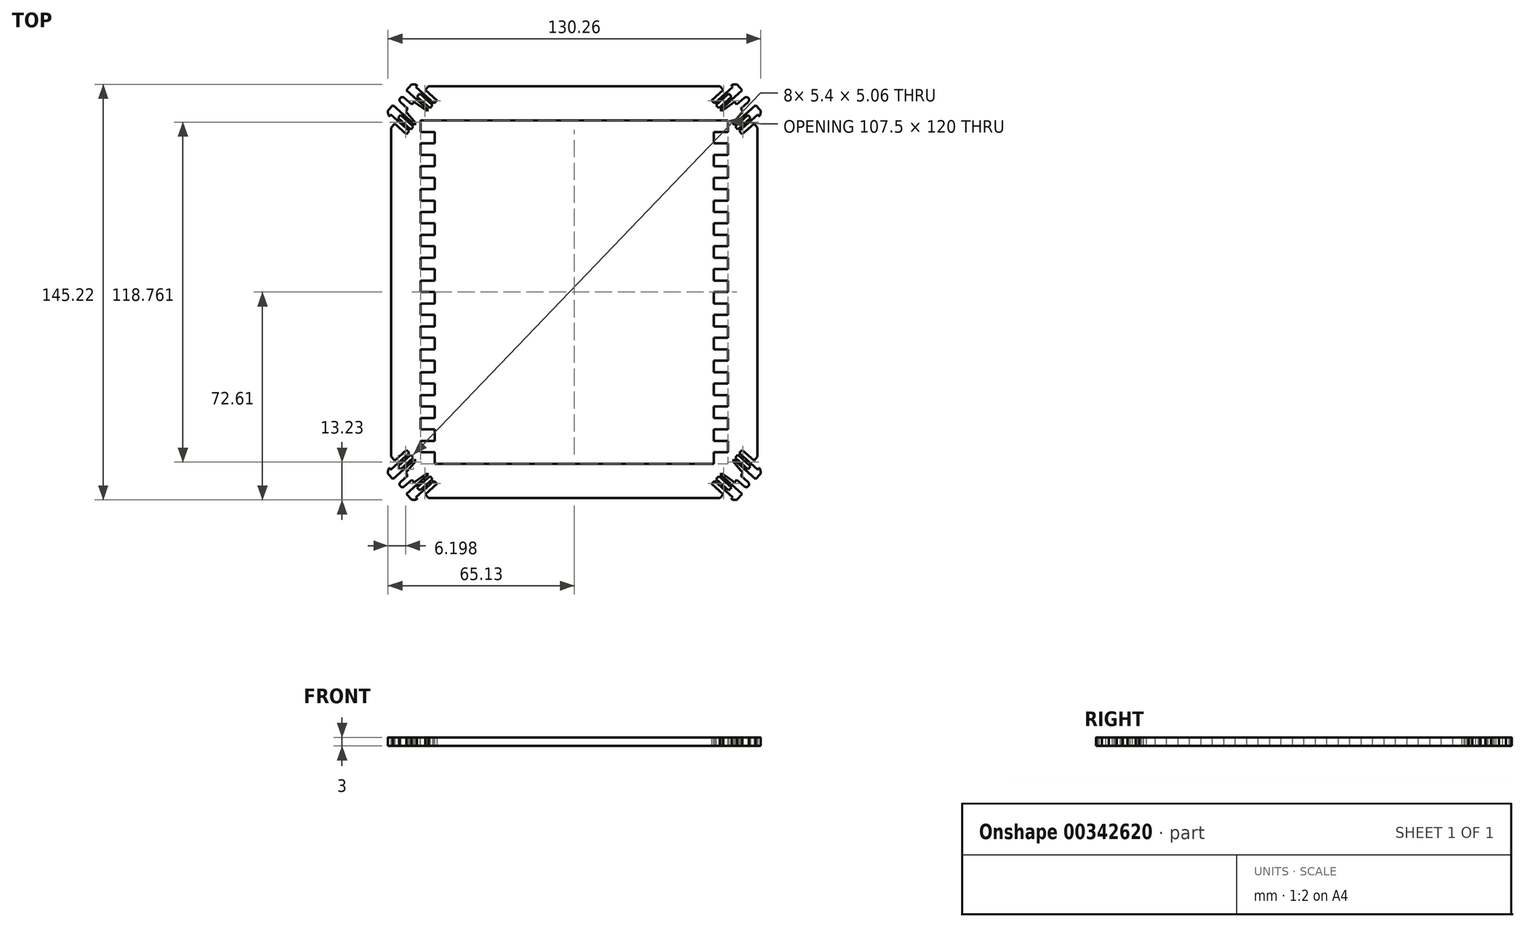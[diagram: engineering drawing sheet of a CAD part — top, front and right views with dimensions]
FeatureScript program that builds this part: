
annotation { "Feature Type Name" : "Feature", "Feature Type Description" : "" }
export const myFeature = defineFeature(function(context is Context, id is Id, definition is map)
    precondition{}
    {
        {
            var Q0;
            Q0=qCreatedBy(makeId("Top.planeOp"),FACE);
            var sketch = newSketch(context, id + "F0", { "sketchPlane" : qUnion([Q0])});
            skLineSegment(sketch, "E0", {"start": v(64, 57.49) * mm, "end": v(64, 0) * mm});
            skLineSegment(sketch, "E1", {"start": v(52.08, 70.72) * mm, "end": v(48, 67.04) * mm});
            skLineSegment(sketch, "E2", {"start": v(48, 67.04) * mm, "end": v(49, 65.92) * mm});
            skLineSegment(sketch, "E3", {"start": v(49, 65.92) * mm, "end": v(55.4, 71.67) * mm});
            skLineSegment(sketch, "E4", {"start": v(58.67, 70.58) * mm, "end": v(51.02, 63.69) * mm});
            skLineSegment(sketch, "E5", {"start": v(51.02, 63.69) * mm, "end": v(51.5, 63.29) * mm});
            skLineSegment(sketch, "E6", {"start": v(51.5, 63.29) * mm, "end": v(56, 66.46) * mm});
            skLineSegment(sketch, "E7", {"start": v(56, 66.46) * mm, "end": v(56.81, 65.55) * mm});
            skLineSegment(sketch, "E8", {"start": v(56.81, 65.55) * mm, "end": v(59.41, 67.89) * mm});
            skLineSegment(sketch, "E9", {"start": v(60.08, 67.15) * mm, "end": v(49.07, 57.23) * mm, "construction": true});
            skLineSegment(sketch, "E10.bottom", {"start": v(49.54, 65.32) * mm, "end": v(50.48, 64.28) * mm});
            skLineSegment(sketch, "E10.top", {"start": v(54, 69.34) * mm, "end": v(54.94, 68.3) * mm});
            skLineSegment(sketch, "E10.left", {"start": v(49.54, 65.32) * mm, "end": v(54, 69.34) * mm});
            skLineSegment(sketch, "E10.right", {"start": v(50.48, 64.28) * mm, "end": v(54.94, 68.3) * mm});
            skLineSegment(sketch, "E11", {"start": v(48, 67.04) * mm, "end": v(52.45, 62.1) * mm, "construction": true});
            skFitSpline(sketch, "E12", {"points": [v(55.4, 71.67) * mm, v(55, 72.26) * mm, v(56.93, 72.51) * mm], "startDerivative": vector(-1.28, 1.46) * mm, "endDerivative": vector(3.75, -1.07) * mm});
            skLineSegment(sketch, "E13", {"start": v(54.62, 75.08) * mm, "end": v(62.29, 66.57) * mm, "construction": true});
            skLineSegment(sketch, "E14", {"start": v(56.93, 72.51) * mm, "end": v(58.67, 70.58) * mm});
            skFitSpline(sketch, "E15.MirrorCS", {"points": [v(64.1, 62.01) * mm, v(64.64, 61.56) * mm, v(65.1, 63.45) * mm], "startDerivative": vector(1.32, -1.42) * mm, "endDerivative": vector(-0.67, 3.84) * mm});
            skLineSegment(sketch, "E16.MirrorCS", {"start": v(58.72, 55.14) * mm, "end": v(57.7, 56.26) * mm});
            skLineSegment(sketch, "E17.MirrorCS", {"start": v(57.17, 56.85) * mm, "end": v(56.23, 57.9) * mm});
            skLineSegment(sketch, "E18.MirrorCS", {"start": v(55.7, 58.49) * mm, "end": v(55.35, 59) * mm});
            skLineSegment(sketch, "E19.MirrorCS", {"start": v(58.72, 55.14) * mm, "end": v(54.27, 60.08) * mm, "construction": true});
            skLineSegment(sketch, "E20.MirrorCS", {"start": v(56.23, 57.9) * mm, "end": v(60.7, 61.9) * mm});
            skLineSegment(sketch, "E21.MirrorCS", {"start": v(62.8, 58.82) * mm, "end": v(58.72, 55.14) * mm});
            skLineSegment(sketch, "E22.MirrorCS", {"start": v(55.35, 59) * mm, "end": v(58.97, 63.15) * mm});
            skLineSegment(sketch, "E23.MirrorCS", {"start": v(63.35, 65.38) * mm, "end": v(55.7, 58.49) * mm});
            skLineSegment(sketch, "E24.MirrorCS", {"start": v(57.7, 56.26) * mm, "end": v(64.1, 62.01) * mm});
            skLineSegment(sketch, "E25.MirrorCS", {"start": v(65.1, 63.45) * mm, "end": v(63.35, 65.38) * mm});
            skLineSegment(sketch, "E26.MirrorCS", {"start": v(58.15, 64.06) * mm, "end": v(60.75, 66.4) * mm});
            skLineSegment(sketch, "E27.MirrorCS", {"start": v(61.63, 60.87) * mm, "end": v(60.7, 61.9) * mm});
            skLineSegment(sketch, "E28.MirrorCS", {"start": v(58.97, 63.15) * mm, "end": v(58.15, 64.06) * mm});
            skLineSegment(sketch, "E29.MirrorCS", {"start": v(57.17, 56.85) * mm, "end": v(61.63, 60.87) * mm});
            skArc(sketch, "E30", {"start": v(59.41, 67.89) * mm, "mid": v(60.83, 67.81) * mm, "end": v(60.75, 66.4) * mm});
            skLineSegment(sketch, "E31.0", {"start": v(54.62, 75.08) * mm, "end": v(56.93, 72.51) * mm, "construction": true});
            skLineSegment(sketch, "E32.0", {"start": v(51.5, 63.29) * mm, "end": v(52.45, 62.1) * mm, "construction": true});
            skLineSegment(sketch, "E33", {"start": v(50.93, 72) * mm, "end": v(0, 72) * mm});
            skLineSegment(sketch, "E34", {"start": v(0, 72) * mm, "end": v(0, 0) * mm});
            skLineSegment(sketch, "E35", {"start": v(0, 0) * mm, "end": v(64, 0) * mm});
            skLineSegment(sketch, "E36", {"start": v(52.08, 70.72) * mm, "end": v(50.93, 72) * mm});
            skLineSegment(sketch, "E37", {"start": v(62.8, 58.82) * mm, "end": v(64, 57.49) * mm});
            skSolve(sketch);
        }
        {
            var Q0;
            Q0 = qSketchRegion(id + "F0", true);
            extrude(context, id + "F1", {"entities" : qUnion([Q0]), "depth" : 3 * mm});
        }
        {
            var Q0;
            Q0=makeQuery(id+"F1.opExtrude","SWEPT_BODY",BODY,{"disambiguationData":[OSD([sQuery(id+"F0.wireOp",EDGE,"E0"),sQuery(id+"F0.wireOp",EDGE,"E1"),sQuery(id+"F0.wireOp",EDGE,"E2"),sQuery(id+"F0.wireOp",EDGE,"E3"),sQuery(id+"F0.wireOp",EDGE,"E4"),sQuery(id+"F0.wireOp",EDGE,"E5"),sQuery(id+"F0.wireOp",EDGE,"E6"),sQuery(id+"F0.wireOp",EDGE,"E7"),sQuery(id+"F0.wireOp",EDGE,"E8"),sQuery(id+"F0.wireOp",EDGE,"E10.bottom"),sQuery(id+"F0.wireOp",EDGE,"E10.top"),sQuery(id+"F0.wireOp",EDGE,"E10.left"),sQuery(id+"F0.wireOp",EDGE,"E10.right"),sQuery(id+"F0.wireOp",EDGE,"E12"),sQuery(id+"F0.wireOp",EDGE,"E14"),sQuery(id+"F0.wireOp",EDGE,"E15.MirrorCS"),sQuery(id+"F0.wireOp",EDGE,"E16.MirrorCS"),sQuery(id+"F0.wireOp",EDGE,"E17.MirrorCS"),sQuery(id+"F0.wireOp",EDGE,"E18.MirrorCS"),sQuery(id+"F0.wireOp",EDGE,"73c64eb1-9053-4ded-a230-a61976290448.MirrorCS"),sQuery(id+"F0.wireOp",EDGE,"E20.MirrorCS"),sQuery(id+"F0.wireOp",EDGE,"E21.MirrorCS"),sQuery(id+"F0.wireOp",EDGE,"E22.MirrorCS"),sQuery(id+"F0.wireOp",EDGE,"E23.MirrorCS"),sQuery(id+"F0.wireOp",EDGE,"E24.MirrorCS"),sQuery(id+"F0.wireOp",EDGE,"E25.MirrorCS"),sQuery(id+"F0.wireOp",EDGE,"E26.MirrorCS"),sQuery(id+"F0.wireOp",EDGE,"E27.MirrorCS"),sQuery(id+"F0.wireOp",EDGE,"E28.MirrorCS"),sQuery(id+"F0.wireOp",EDGE,"E29.MirrorCS"),sQuery(id+"F0.wireOp",EDGE,"E30"),sQuery(id+"F0.wireOp",EDGE,"238d3171-18cf-4664-875a-15b81accc3c9"),sQuery(id+"F0.wireOp",EDGE,"7124a334-57a5-4c12-b1ba-874bc8632110.MirrorC"),sQuery(id+"F0.wireOp",EDGE,"E33"),sQuery(id+"F0.wireOp",EDGE,"44bece61-ac72-4aae-9b04-1ec5777349d3"),sQuery(id+"F0.wireOp",EDGE,"E34"),sQuery(id+"F0.wireOp",EDGE,"E35")])]});
            var Q1;
            Q1=makeQuery(id+"F1.opExtrude","SWEPT_FACE",FACE,{"disambiguationData":[OSD([sQuery(id+"F0.wireOp",EDGE,"E34")])]});
            mirror(context, id + "F2", {"operationType" : NewBodyOperationType.ADD, "entities" : qUnion([Q0]), "mirrorPlane" : qUnion([Q1])});
        }
        {
            var Q0;
            Q0=makeQuery(id+"F1.opExtrude","SWEPT_BODY",BODY,{"disambiguationData":[OSD([sQuery(id+"F0.wireOp",EDGE,"E0"),sQuery(id+"F0.wireOp",EDGE,"E1"),sQuery(id+"F0.wireOp",EDGE,"E2"),sQuery(id+"F0.wireOp",EDGE,"E3"),sQuery(id+"F0.wireOp",EDGE,"E4"),sQuery(id+"F0.wireOp",EDGE,"E5"),sQuery(id+"F0.wireOp",EDGE,"E6"),sQuery(id+"F0.wireOp",EDGE,"E7"),sQuery(id+"F0.wireOp",EDGE,"E8"),sQuery(id+"F0.wireOp",EDGE,"E10.bottom"),sQuery(id+"F0.wireOp",EDGE,"E10.top"),sQuery(id+"F0.wireOp",EDGE,"E10.left"),sQuery(id+"F0.wireOp",EDGE,"E10.right"),sQuery(id+"F0.wireOp",EDGE,"E12"),sQuery(id+"F0.wireOp",EDGE,"E14"),sQuery(id+"F0.wireOp",EDGE,"E15.MirrorCS"),sQuery(id+"F0.wireOp",EDGE,"E16.MirrorCS"),sQuery(id+"F0.wireOp",EDGE,"E17.MirrorCS"),sQuery(id+"F0.wireOp",EDGE,"E18.MirrorCS"),sQuery(id+"F0.wireOp",EDGE,"73c64eb1-9053-4ded-a230-a61976290448.MirrorCS"),sQuery(id+"F0.wireOp",EDGE,"E20.MirrorCS"),sQuery(id+"F0.wireOp",EDGE,"E21.MirrorCS"),sQuery(id+"F0.wireOp",EDGE,"E22.MirrorCS"),sQuery(id+"F0.wireOp",EDGE,"E23.MirrorCS"),sQuery(id+"F0.wireOp",EDGE,"E24.MirrorCS"),sQuery(id+"F0.wireOp",EDGE,"E25.MirrorCS"),sQuery(id+"F0.wireOp",EDGE,"E26.MirrorCS"),sQuery(id+"F0.wireOp",EDGE,"E27.MirrorCS"),sQuery(id+"F0.wireOp",EDGE,"E28.MirrorCS"),sQuery(id+"F0.wireOp",EDGE,"E29.MirrorCS"),sQuery(id+"F0.wireOp",EDGE,"E30"),sQuery(id+"F0.wireOp",EDGE,"238d3171-18cf-4664-875a-15b81accc3c9"),sQuery(id+"F0.wireOp",EDGE,"7124a334-57a5-4c12-b1ba-874bc8632110.MirrorC"),sQuery(id+"F0.wireOp",EDGE,"E33"),sQuery(id+"F0.wireOp",EDGE,"44bece61-ac72-4aae-9b04-1ec5777349d3"),sQuery(id+"F0.wireOp",EDGE,"E34"),sQuery(id+"F0.wireOp",EDGE,"E35")])]});
            var Q1;
            {var subQ0=makeQuery(id+"F1.opExtrude","SWEPT_FACE",FACE,{"disambiguationData":[OSD([sQuery(id+"F0.wireOp",EDGE,"E35")])]});Q1=makeQuery(id+"F2.boolean.opBoolean","MERGE",FACE,{"derivedFrom":[subQ0,makeQuery(id+"F2.opPattern","COPY",FACE,{"derivedFrom":subQ0,"instanceName":"1"})]});}
            mirror(context, id + "F3", {"operationType" : NewBodyOperationType.ADD, "entities" : qUnion([Q0]), "mirrorPlane" : qUnion([Q1])});
        }
        {
            var Q0;
            {var subQ0=makeQuery(id+"F1.opExtrude","CAP_FACE",FACE,{"disambiguationData":[OSD([sQuery(id+"F0.wireOp",EDGE,"E0"),sQuery(id+"F0.wireOp",EDGE,"E1"),sQuery(id+"F0.wireOp",EDGE,"E2"),sQuery(id+"F0.wireOp",EDGE,"E3"),sQuery(id+"F0.wireOp",EDGE,"E4"),sQuery(id+"F0.wireOp",EDGE,"E5"),sQuery(id+"F0.wireOp",EDGE,"E6"),sQuery(id+"F0.wireOp",EDGE,"E7"),sQuery(id+"F0.wireOp",EDGE,"E8"),sQuery(id+"F0.wireOp",EDGE,"E10.bottom"),sQuery(id+"F0.wireOp",EDGE,"E10.top"),sQuery(id+"F0.wireOp",EDGE,"E10.left"),sQuery(id+"F0.wireOp",EDGE,"E10.right"),sQuery(id+"F0.wireOp",EDGE,"E12"),sQuery(id+"F0.wireOp",EDGE,"E14"),sQuery(id+"F0.wireOp",EDGE,"E15.MirrorCS"),sQuery(id+"F0.wireOp",EDGE,"E16.MirrorCS"),sQuery(id+"F0.wireOp",EDGE,"E17.MirrorCS"),sQuery(id+"F0.wireOp",EDGE,"E18.MirrorCS"),sQuery(id+"F0.wireOp",EDGE,"73c64eb1-9053-4ded-a230-a61976290448.MirrorCS"),sQuery(id+"F0.wireOp",EDGE,"E20.MirrorCS"),sQuery(id+"F0.wireOp",EDGE,"E21.MirrorCS"),sQuery(id+"F0.wireOp",EDGE,"E22.MirrorCS"),sQuery(id+"F0.wireOp",EDGE,"E23.MirrorCS"),sQuery(id+"F0.wireOp",EDGE,"E24.MirrorCS"),sQuery(id+"F0.wireOp",EDGE,"E25.MirrorCS"),sQuery(id+"F0.wireOp",EDGE,"E26.MirrorCS"),sQuery(id+"F0.wireOp",EDGE,"E27.MirrorCS"),sQuery(id+"F0.wireOp",EDGE,"E28.MirrorCS"),sQuery(id+"F0.wireOp",EDGE,"E29.MirrorCS"),sQuery(id+"F0.wireOp",EDGE,"E30"),sQuery(id+"F0.wireOp",EDGE,"238d3171-18cf-4664-875a-15b81accc3c9"),sQuery(id+"F0.wireOp",EDGE,"7124a334-57a5-4c12-b1ba-874bc8632110.MirrorC"),sQuery(id+"F0.wireOp",EDGE,"E33"),sQuery(id+"F0.wireOp",EDGE,"44bece61-ac72-4aae-9b04-1ec5777349d3"),sQuery(id+"F0.wireOp",EDGE,"E34"),sQuery(id+"F0.wireOp",EDGE,"E35")])],"isStart":false});var subQ1=makeQuery(id+"F2.boolean.opBoolean","MERGE",FACE,{"derivedFrom":[subQ0,makeQuery(id+"F2.opPattern","COPY",FACE,{"derivedFrom":subQ0,"instanceName":"1"})]});Q0=makeQuery(id+"F3.boolean.opBoolean","MERGE",FACE,{"derivedFrom":[subQ1,makeQuery(id+"F3.opPattern","COPY",FACE,{"derivedFrom":subQ1,"instanceName":"1"})]});}
            var sketch = newSketch(context, id + "F4", { "sketchPlane" : qUnion([Q0])});
            skLineSegment(sketch, "E38.bottom", {"start": v(53.75, 60) * mm, "end": v(-53.75, 60) * mm});
            skLineSegment(sketch, "E38.top", {"start": v(53.75, -60) * mm, "end": v(-53.75, -60) * mm});
            skLineSegment(sketch, "E38.left", {"start": v(53.75, 60) * mm, "end": v(53.75, -60) * mm});
            skLineSegment(sketch, "E38.right", {"start": v(-53.75, 60) * mm, "end": v(-53.75, -60) * mm});
            skPoint(sketch, "E38.middle", {"position": v(0, 0) * mm});
            skSolve(sketch);
        }
        {
            var Q0;
            Q0 = qSketchRegion(id + "F4", true);
            extrude(context, id + "F5", {"entities" : qUnion([Q0]), "operationType" : NewBodyOperationType.REMOVE, "oppositeDirection" : true, "depth" : 3 * mm});
        }
        {
            var Q0;
            {var subQ0=makeQuery(id+"F1.opExtrude","CAP_FACE",FACE,{"disambiguationData":[OSD([sQuery(id+"F0.wireOp",EDGE,"E0"),sQuery(id+"F0.wireOp",EDGE,"E1"),sQuery(id+"F0.wireOp",EDGE,"E2"),sQuery(id+"F0.wireOp",EDGE,"E3"),sQuery(id+"F0.wireOp",EDGE,"E4"),sQuery(id+"F0.wireOp",EDGE,"E5"),sQuery(id+"F0.wireOp",EDGE,"E6"),sQuery(id+"F0.wireOp",EDGE,"E7"),sQuery(id+"F0.wireOp",EDGE,"E8"),sQuery(id+"F0.wireOp",EDGE,"E10.bottom"),sQuery(id+"F0.wireOp",EDGE,"E10.top"),sQuery(id+"F0.wireOp",EDGE,"E10.left"),sQuery(id+"F0.wireOp",EDGE,"E10.right"),sQuery(id+"F0.wireOp",EDGE,"E12"),sQuery(id+"F0.wireOp",EDGE,"E14"),sQuery(id+"F0.wireOp",EDGE,"E15.MirrorCS"),sQuery(id+"F0.wireOp",EDGE,"E16.MirrorCS"),sQuery(id+"F0.wireOp",EDGE,"E17.MirrorCS"),sQuery(id+"F0.wireOp",EDGE,"E18.MirrorCS"),sQuery(id+"F0.wireOp",EDGE,"E20.MirrorCS"),sQuery(id+"F0.wireOp",EDGE,"E21.MirrorCS"),sQuery(id+"F0.wireOp",EDGE,"E22.MirrorCS"),sQuery(id+"F0.wireOp",EDGE,"E23.MirrorCS"),sQuery(id+"F0.wireOp",EDGE,"E24.MirrorCS"),sQuery(id+"F0.wireOp",EDGE,"E25.MirrorCS"),sQuery(id+"F0.wireOp",EDGE,"E26.MirrorCS"),sQuery(id+"F0.wireOp",EDGE,"E27.MirrorCS"),sQuery(id+"F0.wireOp",EDGE,"E28.MirrorCS"),sQuery(id+"F0.wireOp",EDGE,"E29.MirrorCS"),sQuery(id+"F0.wireOp",EDGE,"E30"),sQuery(id+"F0.wireOp",EDGE,"238d3171-18cf-4664-875a-15b81accc3c9"),sQuery(id+"F0.wireOp",EDGE,"7124a334-57a5-4c12-b1ba-874bc8632110.MirrorC"),sQuery(id+"F0.wireOp",EDGE,"E33"),sQuery(id+"F0.wireOp",EDGE,"E34"),sQuery(id+"F0.wireOp",EDGE,"E35"),sQuery(id+"F0.wireOp",EDGE,"E36"),sQuery(id+"F0.wireOp",EDGE,"E37")])],"isStart":false});var subQ1=makeQuery(id+"F2.boolean.opBoolean","MERGE",FACE,{"derivedFrom":[subQ0,makeQuery(id+"F2.opPattern","COPY",FACE,{"derivedFrom":subQ0,"instanceName":"1"})]});Q0=makeQuery(id+"F3.boolean.opBoolean","MERGE",FACE,{"derivedFrom":[subQ1,makeQuery(id+"F3.opPattern","COPY",FACE,{"derivedFrom":subQ1,"instanceName":"1"})]});}
            var sketch = newSketch(context, id + "F6", { "sketchPlane" : qUnion([Q0])});
            skPoint(sketch, "E39.middle", {"position": v(0, 0) * mm});
            skLineSegment(sketch, "E40.bottom", {"start": v(-53.75, -60) * mm, "end": v(-48.75, -60) * mm});
            skLineSegment(sketch, "E40.top", {"start": v(-53.75, -56) * mm, "end": v(-48.75, -56) * mm});
            skLineSegment(sketch, "E40.left", {"start": v(-53.75, -60) * mm, "end": v(-53.75, -56) * mm});
            skLineSegment(sketch, "E40.right", {"start": v(-48.75, -60) * mm, "end": v(-48.75, -56) * mm});
            skLineSegment(sketch, "E41.0.1.0", {"start": v(-48.75, -52) * mm, "end": v(-48.75, -48) * mm});
            skLineSegment(sketch, "E41.0.1.1", {"start": v(-53.75, -48) * mm, "end": v(-48.75, -48) * mm});
            skLineSegment(sketch, "E41.0.1.2", {"start": v(-53.75, -52) * mm, "end": v(-53.75, -48) * mm});
            skLineSegment(sketch, "E41.0.1.3", {"start": v(-53.75, -52) * mm, "end": v(-48.75, -52) * mm});
            skLineSegment(sketch, "E41.0.2.0", {"start": v(-48.75, -44) * mm, "end": v(-48.75, -40) * mm});
            skLineSegment(sketch, "E41.0.2.1", {"start": v(-53.75, -40) * mm, "end": v(-48.75, -40) * mm});
            skLineSegment(sketch, "E41.0.2.2", {"start": v(-53.75, -44) * mm, "end": v(-53.75, -40) * mm});
            skLineSegment(sketch, "E41.0.2.3", {"start": v(-53.75, -44) * mm, "end": v(-48.75, -44) * mm});
            skLineSegment(sketch, "E41.0.3.0", {"start": v(-48.75, -36) * mm, "end": v(-48.75, -32) * mm});
            skLineSegment(sketch, "E41.0.3.1", {"start": v(-53.75, -32) * mm, "end": v(-48.75, -32) * mm});
            skLineSegment(sketch, "E41.0.3.2", {"start": v(-53.75, -36) * mm, "end": v(-53.75, -32) * mm});
            skLineSegment(sketch, "E41.0.3.3", {"start": v(-53.75, -36) * mm, "end": v(-48.75, -36) * mm});
            skLineSegment(sketch, "E41.0.4.0", {"start": v(-48.75, -28) * mm, "end": v(-48.75, -24) * mm});
            skLineSegment(sketch, "E41.0.4.1", {"start": v(-53.75, -24) * mm, "end": v(-48.75, -24) * mm});
            skLineSegment(sketch, "E41.0.4.2", {"start": v(-53.75, -28) * mm, "end": v(-53.75, -24) * mm});
            skLineSegment(sketch, "E41.0.4.3", {"start": v(-53.75, -28) * mm, "end": v(-48.75, -28) * mm});
            skLineSegment(sketch, "E41.0.5.0", {"start": v(-48.75, -20) * mm, "end": v(-48.75, -16) * mm});
            skLineSegment(sketch, "E41.0.5.1", {"start": v(-53.75, -16) * mm, "end": v(-48.75, -16) * mm});
            skLineSegment(sketch, "E41.0.5.2", {"start": v(-53.75, -20) * mm, "end": v(-53.75, -16) * mm});
            skLineSegment(sketch, "E41.0.5.3", {"start": v(-53.75, -20) * mm, "end": v(-48.75, -20) * mm});
            skLineSegment(sketch, "E41.0.6.0", {"start": v(-48.75, -12) * mm, "end": v(-48.75, -8) * mm});
            skLineSegment(sketch, "E41.0.6.1", {"start": v(-53.75, -8) * mm, "end": v(-48.75, -8) * mm});
            skLineSegment(sketch, "E41.0.6.2", {"start": v(-53.75, -12) * mm, "end": v(-53.75, -8) * mm});
            skLineSegment(sketch, "E41.0.6.3", {"start": v(-53.75, -12) * mm, "end": v(-48.75, -12) * mm});
            skLineSegment(sketch, "E41.0.7.0", {"start": v(-48.75, -4) * mm, "end": v(-48.75, 0) * mm});
            skLineSegment(sketch, "E41.0.7.1", {"start": v(-53.75, 0) * mm, "end": v(-48.75, 0) * mm});
            skLineSegment(sketch, "E41.0.7.2", {"start": v(-53.75, -4) * mm, "end": v(-53.75, 0) * mm});
            skLineSegment(sketch, "E41.0.7.3", {"start": v(-53.75, -4) * mm, "end": v(-48.75, -4) * mm});
            skLineSegment(sketch, "E41.0.8.0", {"start": v(-48.75, 4) * mm, "end": v(-48.75, 8) * mm});
            skLineSegment(sketch, "E41.0.8.1", {"start": v(-53.75, 8) * mm, "end": v(-48.75, 8) * mm});
            skLineSegment(sketch, "E41.0.8.2", {"start": v(-53.75, 4) * mm, "end": v(-53.75, 8) * mm});
            skLineSegment(sketch, "E41.0.8.3", {"start": v(-53.75, 4) * mm, "end": v(-48.75, 4) * mm});
            skLineSegment(sketch, "E41.0.9.0", {"start": v(-48.75, 12) * mm, "end": v(-48.75, 16) * mm});
            skLineSegment(sketch, "E41.0.9.1", {"start": v(-53.75, 16) * mm, "end": v(-48.75, 16) * mm});
            skLineSegment(sketch, "E41.0.9.2", {"start": v(-53.75, 12) * mm, "end": v(-53.75, 16) * mm});
            skLineSegment(sketch, "E41.0.9.3", {"start": v(-53.75, 12) * mm, "end": v(-48.75, 12) * mm});
            skLineSegment(sketch, "E41.0.10.0", {"start": v(-48.75, 20) * mm, "end": v(-48.75, 24) * mm});
            skLineSegment(sketch, "E41.0.10.1", {"start": v(-53.75, 24) * mm, "end": v(-48.75, 24) * mm});
            skLineSegment(sketch, "E41.0.10.2", {"start": v(-53.75, 20) * mm, "end": v(-53.75, 24) * mm});
            skLineSegment(sketch, "E41.0.10.3", {"start": v(-53.75, 20) * mm, "end": v(-48.75, 20) * mm});
            skLineSegment(sketch, "E41.0.11.0", {"start": v(-48.75, 28) * mm, "end": v(-48.75, 32) * mm});
            skLineSegment(sketch, "E41.0.11.1", {"start": v(-53.75, 32) * mm, "end": v(-48.75, 32) * mm});
            skLineSegment(sketch, "E41.0.11.2", {"start": v(-53.75, 28) * mm, "end": v(-53.75, 32) * mm});
            skLineSegment(sketch, "E41.0.11.3", {"start": v(-53.75, 28) * mm, "end": v(-48.75, 28) * mm});
            skLineSegment(sketch, "E41.0.12.0", {"start": v(-48.75, 36) * mm, "end": v(-48.75, 40) * mm});
            skLineSegment(sketch, "E41.0.12.1", {"start": v(-53.75, 40) * mm, "end": v(-48.75, 40) * mm});
            skLineSegment(sketch, "E41.0.12.2", {"start": v(-53.75, 36) * mm, "end": v(-53.75, 40) * mm});
            skLineSegment(sketch, "E41.0.12.3", {"start": v(-53.75, 36) * mm, "end": v(-48.75, 36) * mm});
            skLineSegment(sketch, "E41.0.13.0", {"start": v(-48.75, 44) * mm, "end": v(-48.75, 48) * mm});
            skLineSegment(sketch, "E41.0.13.1", {"start": v(-53.75, 48) * mm, "end": v(-48.75, 48) * mm});
            skLineSegment(sketch, "E41.0.13.2", {"start": v(-53.75, 44) * mm, "end": v(-53.75, 48) * mm});
            skLineSegment(sketch, "E41.0.13.3", {"start": v(-53.75, 44) * mm, "end": v(-48.75, 44) * mm});
            skLineSegment(sketch, "E41.0.14.0", {"start": v(-48.75, 52) * mm, "end": v(-48.75, 56) * mm});
            skLineSegment(sketch, "E41.0.14.1", {"start": v(-53.75, 56) * mm, "end": v(-48.75, 56) * mm});
            skLineSegment(sketch, "E41.0.14.2", {"start": v(-53.75, 52) * mm, "end": v(-53.75, 56) * mm});
            skLineSegment(sketch, "E41.0.14.3", {"start": v(-53.75, 52) * mm, "end": v(-48.75, 52) * mm});
            skLineSegment(sketch, "E41.1.0.0", {"start": v(53.75, -60) * mm, "end": v(53.75, -56) * mm});
            skLineSegment(sketch, "E41.1.0.1", {"start": v(48.75, -56) * mm, "end": v(53.75, -56) * mm});
            skLineSegment(sketch, "E41.1.0.2", {"start": v(48.75, -60) * mm, "end": v(48.75, -56) * mm});
            skLineSegment(sketch, "E41.1.0.3", {"start": v(48.75, -60) * mm, "end": v(53.75, -60) * mm});
            skLineSegment(sketch, "E41.1.1.0", {"start": v(53.75, -52) * mm, "end": v(53.75, -48) * mm});
            skLineSegment(sketch, "E41.1.1.1", {"start": v(48.75, -48) * mm, "end": v(53.75, -48) * mm});
            skLineSegment(sketch, "E41.1.1.2", {"start": v(48.75, -52) * mm, "end": v(48.75, -48) * mm});
            skLineSegment(sketch, "E41.1.1.3", {"start": v(48.75, -52) * mm, "end": v(53.75, -52) * mm});
            skLineSegment(sketch, "E41.1.2.0", {"start": v(53.75, -44) * mm, "end": v(53.75, -40) * mm});
            skLineSegment(sketch, "E41.1.2.1", {"start": v(48.75, -40) * mm, "end": v(53.75, -40) * mm});
            skLineSegment(sketch, "E41.1.2.2", {"start": v(48.75, -44) * mm, "end": v(48.75, -40) * mm});
            skLineSegment(sketch, "E41.1.2.3", {"start": v(48.75, -44) * mm, "end": v(53.75, -44) * mm});
            skLineSegment(sketch, "E41.1.3.0", {"start": v(53.75, -36) * mm, "end": v(53.75, -32) * mm});
            skLineSegment(sketch, "E41.1.3.1", {"start": v(48.75, -32) * mm, "end": v(53.75, -32) * mm});
            skLineSegment(sketch, "E41.1.3.2", {"start": v(48.75, -36) * mm, "end": v(48.75, -32) * mm});
            skLineSegment(sketch, "E41.1.3.3", {"start": v(48.75, -36) * mm, "end": v(53.75, -36) * mm});
            skLineSegment(sketch, "E41.1.4.0", {"start": v(53.75, -28) * mm, "end": v(53.75, -24) * mm});
            skLineSegment(sketch, "E41.1.4.1", {"start": v(48.75, -24) * mm, "end": v(53.75, -24) * mm});
            skLineSegment(sketch, "E41.1.4.2", {"start": v(48.75, -28) * mm, "end": v(48.75, -24) * mm});
            skLineSegment(sketch, "E41.1.4.3", {"start": v(48.75, -28) * mm, "end": v(53.75, -28) * mm});
            skLineSegment(sketch, "E41.1.5.0", {"start": v(53.75, -20) * mm, "end": v(53.75, -16) * mm});
            skLineSegment(sketch, "E41.1.5.1", {"start": v(48.75, -16) * mm, "end": v(53.75, -16) * mm});
            skLineSegment(sketch, "E41.1.5.2", {"start": v(48.75, -20) * mm, "end": v(48.75, -16) * mm});
            skLineSegment(sketch, "E41.1.5.3", {"start": v(48.75, -20) * mm, "end": v(53.75, -20) * mm});
            skLineSegment(sketch, "E41.1.6.0", {"start": v(53.75, -12) * mm, "end": v(53.75, -8) * mm});
            skLineSegment(sketch, "E41.1.6.1", {"start": v(48.75, -8) * mm, "end": v(53.75, -8) * mm});
            skLineSegment(sketch, "E41.1.6.2", {"start": v(48.75, -12) * mm, "end": v(48.75, -8) * mm});
            skLineSegment(sketch, "E41.1.6.3", {"start": v(48.75, -12) * mm, "end": v(53.75, -12) * mm});
            skLineSegment(sketch, "E41.1.7.0", {"start": v(53.75, -4) * mm, "end": v(53.75, 0) * mm});
            skLineSegment(sketch, "E41.1.7.1", {"start": v(48.75, 0) * mm, "end": v(53.75, 0) * mm});
            skLineSegment(sketch, "E41.1.7.2", {"start": v(48.75, -4) * mm, "end": v(48.75, 0) * mm});
            skLineSegment(sketch, "E41.1.7.3", {"start": v(48.75, -4) * mm, "end": v(53.75, -4) * mm});
            skLineSegment(sketch, "E41.1.8.0", {"start": v(53.75, 4) * mm, "end": v(53.75, 8) * mm});
            skLineSegment(sketch, "E41.1.8.1", {"start": v(48.75, 8) * mm, "end": v(53.75, 8) * mm});
            skLineSegment(sketch, "E41.1.8.2", {"start": v(48.75, 4) * mm, "end": v(48.75, 8) * mm});
            skLineSegment(sketch, "E41.1.8.3", {"start": v(48.75, 4) * mm, "end": v(53.75, 4) * mm});
            skLineSegment(sketch, "E41.1.9.0", {"start": v(53.75, 12) * mm, "end": v(53.75, 16) * mm});
            skLineSegment(sketch, "E41.1.9.1", {"start": v(48.75, 16) * mm, "end": v(53.75, 16) * mm});
            skLineSegment(sketch, "E41.1.9.2", {"start": v(48.75, 12) * mm, "end": v(48.75, 16) * mm});
            skLineSegment(sketch, "E41.1.9.3", {"start": v(48.75, 12) * mm, "end": v(53.75, 12) * mm});
            skLineSegment(sketch, "E41.1.10.0", {"start": v(53.75, 20) * mm, "end": v(53.75, 24) * mm});
            skLineSegment(sketch, "E41.1.10.1", {"start": v(48.75, 24) * mm, "end": v(53.75, 24) * mm});
            skLineSegment(sketch, "E41.1.10.2", {"start": v(48.75, 20) * mm, "end": v(48.75, 24) * mm});
            skLineSegment(sketch, "E41.1.10.3", {"start": v(48.75, 20) * mm, "end": v(53.75, 20) * mm});
            skLineSegment(sketch, "E41.1.11.0", {"start": v(53.75, 28) * mm, "end": v(53.75, 32) * mm});
            skLineSegment(sketch, "E41.1.11.1", {"start": v(48.75, 32) * mm, "end": v(53.75, 32) * mm});
            skLineSegment(sketch, "E41.1.11.2", {"start": v(48.75, 28) * mm, "end": v(48.75, 32) * mm});
            skLineSegment(sketch, "E41.1.11.3", {"start": v(48.75, 28) * mm, "end": v(53.75, 28) * mm});
            skLineSegment(sketch, "E41.1.12.0", {"start": v(53.75, 36) * mm, "end": v(53.75, 40) * mm});
            skLineSegment(sketch, "E41.1.12.1", {"start": v(48.75, 40) * mm, "end": v(53.75, 40) * mm});
            skLineSegment(sketch, "E41.1.12.2", {"start": v(48.75, 36) * mm, "end": v(48.75, 40) * mm});
            skLineSegment(sketch, "E41.1.12.3", {"start": v(48.75, 36) * mm, "end": v(53.75, 36) * mm});
            skLineSegment(sketch, "E41.1.13.0", {"start": v(53.75, 44) * mm, "end": v(53.75, 48) * mm});
            skLineSegment(sketch, "E41.1.13.1", {"start": v(48.75, 48) * mm, "end": v(53.75, 48) * mm});
            skLineSegment(sketch, "E41.1.13.2", {"start": v(48.75, 44) * mm, "end": v(48.75, 48) * mm});
            skLineSegment(sketch, "E41.1.13.3", {"start": v(48.75, 44) * mm, "end": v(53.75, 44) * mm});
            skLineSegment(sketch, "E41.1.14.0", {"start": v(53.75, 52) * mm, "end": v(53.75, 56) * mm});
            skLineSegment(sketch, "E41.1.14.1", {"start": v(48.75, 56) * mm, "end": v(53.75, 56) * mm});
            skLineSegment(sketch, "E41.1.14.2", {"start": v(48.75, 52) * mm, "end": v(48.75, 56) * mm});
            skLineSegment(sketch, "E41.1.14.3", {"start": v(48.75, 52) * mm, "end": v(53.75, 52) * mm});
            skLineSegment(sketch, "E41.direction1", {"start": v(-53.75, -60) * mm, "end": v(48.75, -60) * mm, "construction": true});
            skLineSegment(sketch, "E41.direction2", {"start": v(-53.75, -60) * mm, "end": v(-53.75, -52) * mm, "construction": true});
            skSolve(sketch);
        }
        {
            var Q0;
            Q0 = qSketchRegion(id + "F6", true);
            extrude(context, id + "F7", {"entities" : qUnion([Q0]), "operationType" : NewBodyOperationType.ADD, "oppositeDirection" : true, "depth" : 3 * mm});
        }
    });
